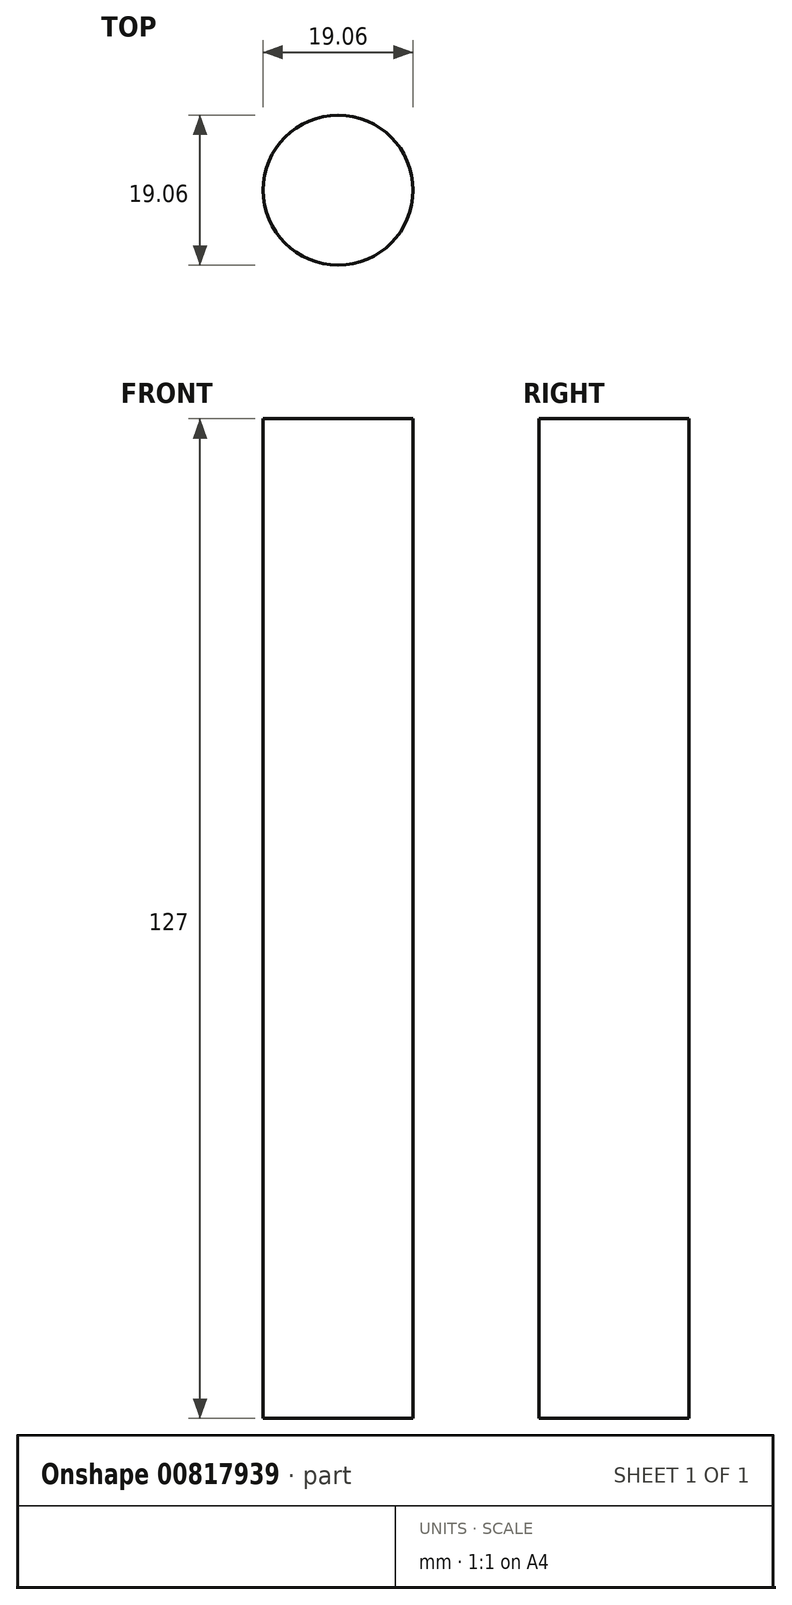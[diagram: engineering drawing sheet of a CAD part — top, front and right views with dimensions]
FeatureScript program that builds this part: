
annotation { "Feature Type Name" : "Feature", "Feature Type Description" : "" }
export const myFeature = defineFeature(function(context is Context, id is Id, definition is map)
    precondition{}
    {
        {
            var Q0;
            Q0=qCreatedBy(makeId("Top.planeOp"),FACE);
            var sketch = newSketch(context, id + "F0", { "sketchPlane" : qUnion([Q0])});
            skCircle(sketch, "E0", {"center": v(0, 0) * mm, "radius": 9.53 * mm});
            skSolve(sketch);
        }
        {
            var Q0;
            Q0 = qSketchRegion(id + "F0", true);
            extrude(context, id + "F1", {"entities" : qUnion([Q0]), "depth" : 127 * mm, "offsetDistance" : 25.4 * mm});
        }
    });
